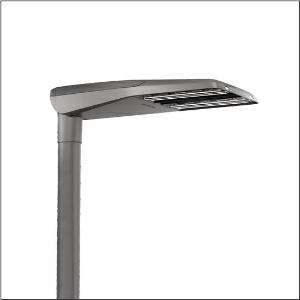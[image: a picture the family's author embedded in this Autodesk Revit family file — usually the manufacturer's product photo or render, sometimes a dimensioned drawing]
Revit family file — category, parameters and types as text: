
# Revit family: streetlight_sl_11_iq_midi___st1_0st0_5_5xc3j51f08me_a600
name_source: partatom
category: Lighting Fixtures
units: mm (PartAtom-declared; Revit-internal decimal feet)

## family parameters
Cut with Voids When Loaded = No
Host = Face
Light Source = No
Part Type = Normal
Room Calculation Point = No
Round Connector Dimension = Use Diameter
Shared = No

## types (1)
- --- (1 x LED, 17650 lm, 124.7 W, 3000K)
    Apparent Load = 125 VA
    CIE Flux Codes = 35 68 96 100 100
    Color Rendering = 70
    Color Temperature = 3000K
    Default Elevation = 1800 mm
    Description = Streetlight SL 11 iQ midi, mast luminaire, primary light control with 3 zone facetted reflector, of plastic, silver coated, highly specular, primary optical cover: cover, of PMMA, transparent, light distribution: ST1.0ST0.5, light emission: direct distribution, primary light characteristic: asymmetric, installation type: post-top, side-entry, lamps: LED, High Power LED, rated values: 17.650lm | 124,7W | 141,5lm/W (begin service life); end service life: 17.650lm | 132,2W; at 50% lumin. flux: 8.825lm | 57,2W | 154,3lm/W, colour temperature: 3000K, colour rendering: CRI > 70, light colour: 730, light setting 1 begin service life: 100% | 17.650lm | 124,7W | 141,5lm/W | 3.000K, light setting 1 end service life: 132,2W, further light settings possible, control: Street-Remote, Auto-Match, Temp-Guard, Lumen-Switch, Night-Set, Smart-Wire, Light-Fading, Desk-Remote (wireless, voltage-free reading and setting of iQ features in the workshop via application-optimized NFC function/RFID function), optimised constant luminous flux control (CLO 2.0), with cable H07RN-F 5x 1.5mm², mains connection: 230..240V, AC, 50/60Hz, connection cable pre-assembled, cable length: 12,5m, luminaire housing, of diecast aluminium, powder-coated, Siteco® metallic grey (DB 702S), please order mast flange separately, inclination adjustable without tools: 0°, 5°, 10°, 15° (post-top) | 0°, -5°, -10°, -15° (side-entry), sealing non-destructively replaceable, multi-level sealing system, length: 780mm, width: 376mm, height: 118mm, mast flange for spigot size: 42mm (side-entry): 5XC10008XM4, 60/48mm (side-entry/post-top): 5XC10108XM2, 76/60mm (side-entry/post-top): 5XC10108XM1, equipment: Power, protection rating (complete): IP66, insulation class (complete): insulation class II (safety insulation), certification: CE, ENEC, ENEC+, VDE, impact resistance: IK10, permissible operating ambient temperature for outdoor applications: -25..+50°C, standard-compliant lighting for roads and squares, Environmental Product Declaration (EPD) tested and certified by an independent institute, packaging unit: 1 piece

Light Distribution: ST1.0ST0.5
    Height = 118 mm
    Lamp = 1 x LED
    Lamp Light Flux = 17650 lm
    Lamp Power = 124.7 W
    Lamp count = 1
    Length = 780 mm
    Luminous efficacy = 142 lm/W
    Manufacturer = Siteco
    ModVariant = No
    Model = 5XC3J51F08ME
    Number of Poles = 1
    OnlyDefault = Yes
    Power Factor = 1
    Product Name = Streetlight SL 11 iQ midi | ST1.0ST0.5
    Product group = mast luminaire | pylon top
    ProductGroupID = 6100
    Protection Class = Protection class II
    Protection Degree = IP 66
    RLX_Detail_Level = 1
    RLX_Emergency_Light_Flux = 0 lm
    RLX_Emergency_Type = 0
    RLX_Emergency_Type_DB = No
    RlxData = <blob elided: 70829 chars, md5=1bcf6561>
    Socket = socket
    Standby Power = 0 W
    System Light Flux = 17650 lm
    System Power = 125 W
    Type Comments = factory setting: luminous flux: 100 % | dim-lin: 254 | 557 mA
    Type Image = l_1005960.jpg
    URL = http://relux.com
    VarID = @adj_050047
    Voltage = 0 V
    Weight = 0.00 kg
    Width = 376 mm

## geometry (parser evidence)
native form markers: Blend x4, Sweep x7
no freeform markers — native parametric forms only
